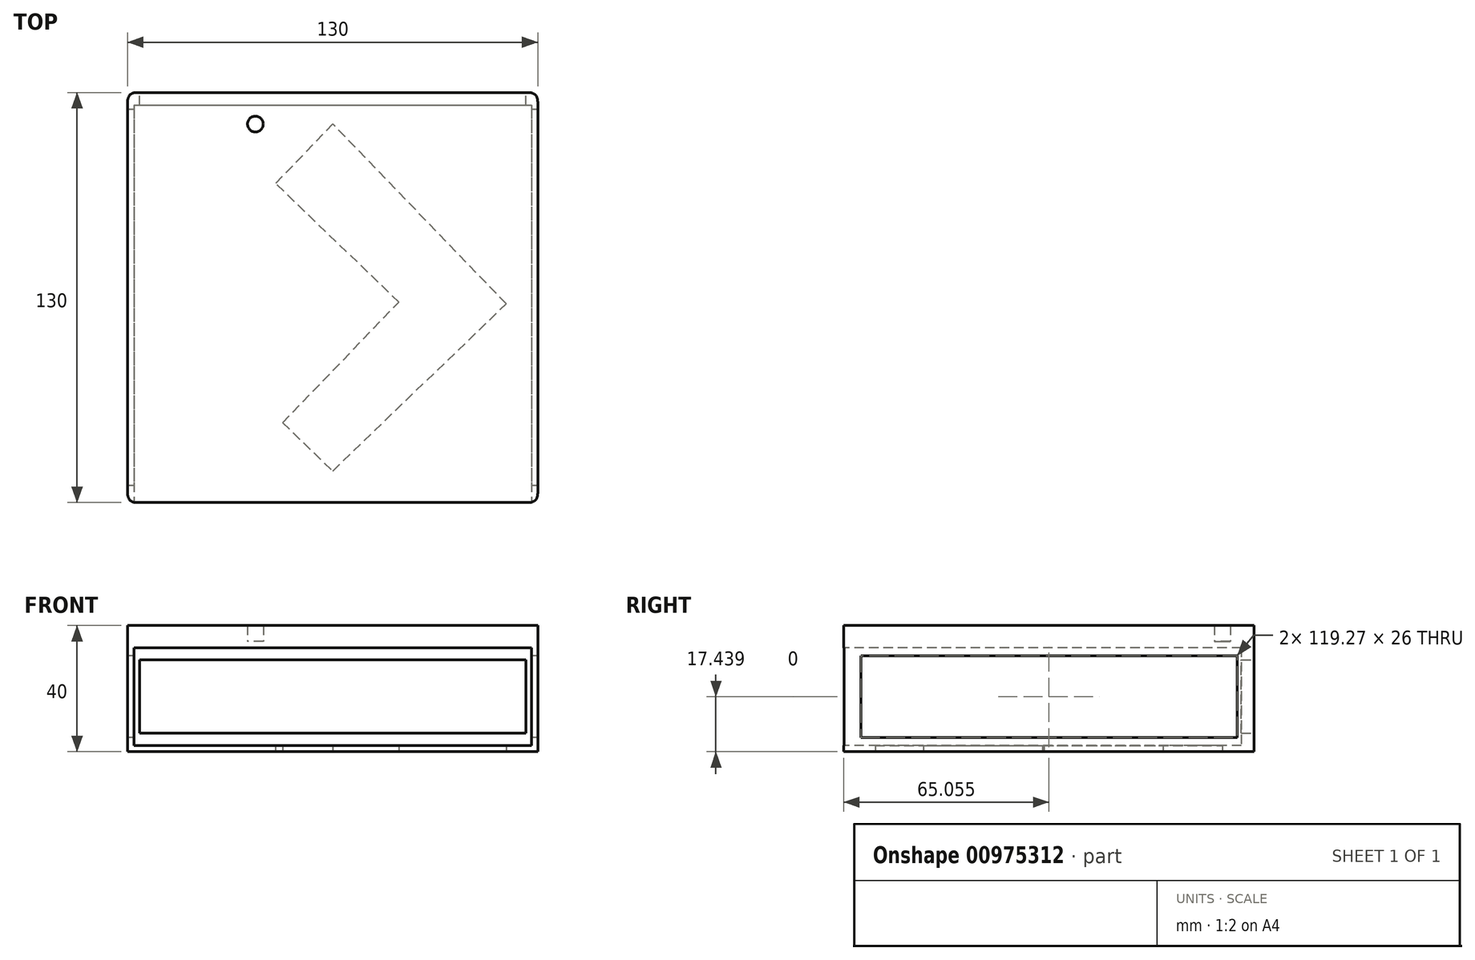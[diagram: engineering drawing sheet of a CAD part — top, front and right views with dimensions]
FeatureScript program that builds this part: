
annotation { "Feature Type Name" : "Feature", "Feature Type Description" : "" }
export const myFeature = defineFeature(function(context is Context, id is Id, definition is map)
    precondition{}
    {
        {
            var Q0;
            Q0=qCreatedBy(makeId("Top.planeOp"),FACE);
            var sketch = newSketch(context, id + "F0", { "sketchPlane" : qUnion([Q0])});
            skLineSegment(sketch, "E0.bottom", {"start": v(-63, 66.16) * mm, "end": v(67, 66.16) * mm});
            skLineSegment(sketch, "E0.top", {"start": v(-63, -63.84) * mm, "end": v(67, -63.84) * mm});
            skLineSegment(sketch, "E0.left", {"start": v(-63, 66.16) * mm, "end": v(-63, -63.84) * mm});
            skLineSegment(sketch, "E0.right", {"start": v(67, 66.16) * mm, "end": v(67, -63.84) * mm});
            skSolve(sketch);
        }
        {
            var Q0;
            Q0=makeQuery(id+"F0.imprint","IMPRINT",FACE,{"disambiguationData":[TD([[makeQuery(id+"F0.imprint","IMPRINT",EDGE,{"derivedFrom":sQuery(id+"F0.wireOp",EDGE,"E0.bottom")}),-1.0]])]});
            extrude(context, id + "F1", {"entities" : qUnion([Q0]), "endBound" : BoundingType.SYMMETRIC, "depth" : 35 * mm, "offsetDistance" : 25 * mm});
        }
        {
            var Q0;
            Q0=makeQuery(id+"F1.opExtrude","SWEPT_FACE",FACE,{"disambiguationData":[OSD([sQuery(id+"F0.wireOp",EDGE,"E0.top")])]});
            var sketch = newSketch(context, id + "F2", { "sketchPlane" : qUnion([Q0])});
            skLineSegment(sketch, "E1.bottom", {"start": v(-61, 15.5) * mm, "end": v(65, 15.5) * mm});
            skLineSegment(sketch, "E1.top", {"start": v(-61, -15.5) * mm, "end": v(65, -15.5) * mm});
            skLineSegment(sketch, "E1.left", {"start": v(-61, 15.5) * mm, "end": v(-61, -15.5) * mm});
            skLineSegment(sketch, "E1.right", {"start": v(65, 15.5) * mm, "end": v(65, -15.5) * mm});
            skSolve(sketch);
        }
        {
            var Q0;
            Q0=makeQuery(id+"F2.imprint","IMPRINT",FACE,{"disambiguationData":[TD([[makeQuery(id+"F2.imprint","IMPRINT",EDGE,{"derivedFrom":sQuery(id+"F2.wireOp",EDGE,"E1.bottom")}),-1.0]])]});
            extrude(context, id + "F3", {"entities" : qUnion([Q0]), "operationType" : NewBodyOperationType.REMOVE, "oppositeDirection" : true, "depth" : 126 * mm, "offsetDistance" : 25 * mm});
        }
        {
            var Q0;
            Q0=makeQuery(id+"F1.opExtrude","CAP_FACE",FACE,{"disambiguationData":[OSD([sQuery(id+"F0.wireOp",EDGE,"E0.bottom"),sQuery(id+"F0.wireOp",EDGE,"E0.top"),sQuery(id+"F0.wireOp",EDGE,"E0.left"),sQuery(id+"F0.wireOp",EDGE,"E0.right")])],"isStart":false});
            var sketch = newSketch(context, id + "F4", { "sketchPlane" : qUnion([Q0])});
            skCircle(sketch, "E2", {"center": v(-22.5, -53.84) * mm, "radius": 2.5 * mm});
            skLineSegment(sketch, "E3.bottom", {"start": v(-53, 56.16) * mm, "end": v(57, 56.16) * mm});
            skLineSegment(sketch, "E3.top", {"start": v(-53, -53.84) * mm, "end": v(57, -53.84) * mm});
            skLineSegment(sketch, "E3.left", {"start": v(-53, 56.16) * mm, "end": v(-53, -53.84) * mm});
            skLineSegment(sketch, "E3.right", {"start": v(57, 56.16) * mm, "end": v(57, -53.84) * mm});
            skLineSegment(sketch, "E4.bottom", {"start": v(-63, 66.16) * mm, "end": v(67, 66.16) * mm});
            skLineSegment(sketch, "E4.top", {"start": v(-63, -63.84) * mm, "end": v(67, -63.84) * mm});
            skLineSegment(sketch, "E4.left", {"start": v(-63, 66.16) * mm, "end": v(-63, -63.84) * mm});
            skLineSegment(sketch, "E4.right", {"start": v(67, 66.16) * mm, "end": v(67, -63.84) * mm});
            skCircle(sketch, "E5", {"center": v(-22.5, 56.16) * mm, "radius": 2.5 * mm});
            skCircle(sketch, "E6", {"center": v(22.5, 56.16) * mm, "radius": 2.5 * mm});
            skCircle(sketch, "E7", {"center": v(22.5, -53.84) * mm, "radius": 2.5 * mm});
            skCircle(sketch, "E8", {"center": v(57.01, -53.81) * mm, "radius": 2.5 * mm});
            skCircle(sketch, "E9", {"center": v(-53, 56.17) * mm, "radius": 2.5 * mm});
            skCircle(sketch, "E10", {"center": v(57, 56.17) * mm, "radius": 2.5 * mm});
            skCircle(sketch, "E11", {"center": v(-53, -53.84) * mm, "radius": 2.5 * mm});
            skSolve(sketch);
        }
        {
            var Q0;
            Q0=makeQuery(id+"F4.imprint","IMPRINT",FACE,{"disambiguationData":[TD([[makeQuery(id+"F4.imprint","IMPRINT",EDGE,{"derivedFrom":sQuery(id+"F4.wireOp",EDGE,"E2")}),1.0]])]});
            var Q1;
            {var subQ0=sQuery(id+"F4.wireOp",EDGE,"E5");var subQ1=sQuery(id+"F4.wireOp",EDGE,"E3.bottom");var subQ2=makeQuery(id+"F4.imprint","INTERSECT",VERTEX,{"disambiguationData":[OD(0.0)],"derivedFrom":[subQ1,subQ0]});Q1=makeQuery(id+"F4.imprint","IMPRINT",FACE,{"disambiguationData":[TD([[makeQuery(id+"F4.imprint","IMPRINT",EDGE,{"disambiguationData":[TD([[subQ2,-1.0]])],"derivedFrom":subQ1}),1.0]])]});}
            var Q2;
            {var subQ0=sQuery(id+"F4.wireOp",EDGE,"E5");var subQ1=sQuery(id+"F4.wireOp",EDGE,"E3.bottom");var subQ2=makeQuery(id+"F4.imprint","INTERSECT",VERTEX,{"disambiguationData":[OD(0.0)],"derivedFrom":[subQ1,subQ0]});Q2=makeQuery(id+"F4.imprint","IMPRINT",FACE,{"disambiguationData":[TD([[makeQuery(id+"F4.imprint","IMPRINT",EDGE,{"disambiguationData":[TD([[subQ2,-1.0]])],"derivedFrom":subQ1}),-1.0]])]});}
            var Q3;
            {var subQ0=sQuery(id+"F4.wireOp",EDGE,"E6");var subQ1=sQuery(id+"F4.wireOp",EDGE,"E3.bottom");var subQ2=makeQuery(id+"F4.imprint","INTERSECT",VERTEX,{"disambiguationData":[OD(0.0)],"derivedFrom":[subQ1,subQ0]});Q3=makeQuery(id+"F4.imprint","IMPRINT",FACE,{"disambiguationData":[TD([[makeQuery(id+"F4.imprint","IMPRINT",EDGE,{"disambiguationData":[TD([[subQ2,-1.0]])],"derivedFrom":subQ1}),1.0]])]});}
            var Q4;
            {var subQ0=sQuery(id+"F4.wireOp",EDGE,"E6");var subQ1=sQuery(id+"F4.wireOp",EDGE,"E3.bottom");var subQ2=makeQuery(id+"F4.imprint","INTERSECT",VERTEX,{"disambiguationData":[OD(0.0)],"derivedFrom":[subQ1,subQ0]});Q4=makeQuery(id+"F4.imprint","IMPRINT",FACE,{"disambiguationData":[TD([[makeQuery(id+"F4.imprint","IMPRINT",EDGE,{"disambiguationData":[TD([[subQ2,-1.0]])],"derivedFrom":subQ1}),-1.0]])]});}
            var Q5;
            {var subQ0=sQuery(id+"F4.wireOp",EDGE,"E7");var subQ1=sQuery(id+"F4.wireOp",EDGE,"E3.top");var subQ2=makeQuery(id+"F4.imprint","INTERSECT",VERTEX,{"disambiguationData":[OD(0.0)],"derivedFrom":[subQ1,subQ0]});Q5=makeQuery(id+"F4.imprint","IMPRINT",FACE,{"disambiguationData":[TD([[makeQuery(id+"F4.imprint","IMPRINT",EDGE,{"disambiguationData":[TD([[subQ2,-1.0]])],"derivedFrom":subQ1}),-1.0]])]});}
            var Q6;
            {var subQ0=sQuery(id+"F4.wireOp",EDGE,"E7");var subQ1=sQuery(id+"F4.wireOp",EDGE,"E3.top");var subQ2=makeQuery(id+"F4.imprint","INTERSECT",VERTEX,{"disambiguationData":[OD(0.0)],"derivedFrom":[subQ1,subQ0]});Q6=makeQuery(id+"F4.imprint","IMPRINT",FACE,{"disambiguationData":[TD([[makeQuery(id+"F4.imprint","IMPRINT",EDGE,{"disambiguationData":[TD([[subQ2,-1.0]])],"derivedFrom":subQ1}),1.0]])]});}
            var Q7;
            {var subQ0=sQuery(id+"F4.wireOp",EDGE,"E3.right");var subQ1=sQuery(id+"F4.wireOp",EDGE,"E3.bottom");var subQ2=makeQuery(id+"F4.imprint","INTERSECT",VERTEX,{"derivedFrom":[subQ1,subQ0]});Q7=makeQuery(id+"F4.imprint","IMPRINT",FACE,{"disambiguationData":[TD([[makeQuery(id+"F4.imprint","IMPRINT",EDGE,{"disambiguationData":[TD([[subQ2,1.0]])],"derivedFrom":subQ1}),-1.0]])]});}
            var Q8;
            {var subQ0=sQuery(id+"F4.wireOp",EDGE,"E3.right");var subQ1=sQuery(id+"F4.wireOp",EDGE,"E3.bottom");var subQ2=makeQuery(id+"F4.imprint","INTERSECT",VERTEX,{"derivedFrom":[subQ1,subQ0]});Q8=makeQuery(id+"F4.imprint","IMPRINT",FACE,{"disambiguationData":[TD([[makeQuery(id+"F4.imprint","IMPRINT",EDGE,{"disambiguationData":[TD([[subQ2,1.0]])],"derivedFrom":subQ1}),1.0]])]});}
            var Q9;
            {var subQ0=sQuery(id+"F4.wireOp",EDGE,"E3.right");var subQ1=sQuery(id+"F4.wireOp",EDGE,"E3.top");var subQ2=makeQuery(id+"F4.imprint","INTERSECT",VERTEX,{"derivedFrom":[subQ1,subQ0]});Q9=makeQuery(id+"F4.imprint","IMPRINT",FACE,{"disambiguationData":[TD([[makeQuery(id+"F4.imprint","IMPRINT",EDGE,{"disambiguationData":[TD([[subQ2,1.0]])],"derivedFrom":subQ1}),1.0]])]});}
            var Q10;
            {var subQ0=sQuery(id+"F4.wireOp",EDGE,"E3.right");var subQ1=sQuery(id+"F4.wireOp",EDGE,"E3.top");var subQ2=makeQuery(id+"F4.imprint","INTERSECT",VERTEX,{"derivedFrom":[subQ1,subQ0]});Q10=makeQuery(id+"F4.imprint","IMPRINT",FACE,{"disambiguationData":[TD([[makeQuery(id+"F4.imprint","IMPRINT",EDGE,{"disambiguationData":[TD([[subQ2,1.0]])],"derivedFrom":subQ1}),-1.0]])]});}
            var Q11;
            {var subQ0=sQuery(id+"F4.wireOp",EDGE,"E3.left");var subQ1=sQuery(id+"F4.wireOp",EDGE,"E3.top");var subQ2=makeQuery(id+"F4.imprint","INTERSECT",VERTEX,{"derivedFrom":[subQ1,subQ0]});Q11=makeQuery(id+"F4.imprint","IMPRINT",FACE,{"disambiguationData":[TD([[makeQuery(id+"F4.imprint","IMPRINT",EDGE,{"disambiguationData":[TD([[subQ2,-1.0]])],"derivedFrom":subQ1}),-1.0]])]});}
            var Q12;
            {var subQ0=sQuery(id+"F4.wireOp",EDGE,"E3.left");var subQ1=sQuery(id+"F4.wireOp",EDGE,"E3.top");var subQ2=makeQuery(id+"F4.imprint","INTERSECT",VERTEX,{"derivedFrom":[subQ1,subQ0]});Q12=makeQuery(id+"F4.imprint","IMPRINT",FACE,{"disambiguationData":[TD([[makeQuery(id+"F4.imprint","IMPRINT",EDGE,{"disambiguationData":[TD([[subQ2,-1.0]])],"derivedFrom":subQ1}),1.0]])]});}
            var Q13;
            {var subQ0=sQuery(id+"F4.wireOp",EDGE,"E3.left");var subQ1=sQuery(id+"F4.wireOp",EDGE,"E3.bottom");var subQ2=makeQuery(id+"F4.imprint","INTERSECT",VERTEX,{"derivedFrom":[subQ1,subQ0]});Q13=makeQuery(id+"F4.imprint","IMPRINT",FACE,{"disambiguationData":[TD([[makeQuery(id+"F4.imprint","IMPRINT",EDGE,{"disambiguationData":[TD([[subQ2,-1.0]])],"derivedFrom":subQ1}),-1.0]])]});}
            var Q14;
            {var subQ0=sQuery(id+"F4.wireOp",EDGE,"E3.left");var subQ1=sQuery(id+"F4.wireOp",EDGE,"E3.bottom");var subQ2=makeQuery(id+"F4.imprint","INTERSECT",VERTEX,{"derivedFrom":[subQ1,subQ0]});Q14=makeQuery(id+"F4.imprint","IMPRINT",FACE,{"disambiguationData":[TD([[makeQuery(id+"F4.imprint","IMPRINT",EDGE,{"disambiguationData":[TD([[subQ2,-1.0]])],"derivedFrom":subQ1}),1.0]])]});}
            extrude(context, id + "F5", {"entities" : qUnion([Q0, Q1, Q2, Q3, Q4, Q5, Q6, Q7, Q8, Q9, Q10, Q11, Q12, Q13, Q14]), "operationType" : NewBodyOperationType.ADD, "depth" : 5 * mm, "offsetDistance" : 25 * mm});
        }
        {
            var Q0;
            Q0=makeQuery(id+"F1.opExtrude","CAP_FACE",FACE,{"disambiguationData":[OSD([sQuery(id+"F0.wireOp",EDGE,"E0.bottom"),sQuery(id+"F0.wireOp",EDGE,"E0.top"),sQuery(id+"F0.wireOp",EDGE,"E0.left"),sQuery(id+"F0.wireOp",EDGE,"E0.right")])],"isStart":true});
            var sketch = newSketch(context, id + "F6", { "sketchPlane" : qUnion([Q0])});
            skLineSegment(sketch, "E12.bottom", {"start": v(-63, 63.84) * mm, "end": v(67, 63.84) * mm});
            skLineSegment(sketch, "E12.top", {"start": v(-63, -66.16) * mm, "end": v(67, -66.16) * mm});
            skLineSegment(sketch, "E12.left", {"start": v(-63, 63.84) * mm, "end": v(-63, -66.16) * mm});
            skLineSegment(sketch, "E12.right", {"start": v(67, 63.84) * mm, "end": v(67, -66.16) * mm});
            skLineSegment(sketch, "E13.bottom", {"start": v(-53, 53.84) * mm, "end": v(57, 53.84) * mm});
            skLineSegment(sketch, "E13.top", {"start": v(-53, -56.16) * mm, "end": v(57, -56.16) * mm});
            skLineSegment(sketch, "E13.left", {"start": v(-53, 53.84) * mm, "end": v(-53, -56.16) * mm});
            skLineSegment(sketch, "E13.right", {"start": v(57, 53.84) * mm, "end": v(57, -56.16) * mm});
            skLineSegment(sketch, "E14", {"start": v(-53, 0.84) * mm, "end": v(2, 53.84) * mm});
            skLineSegment(sketch, "E15", {"start": v(2, 53.84) * mm, "end": v(57, 0.84) * mm});
            skLineSegment(sketch, "E16", {"start": v(57, 0.84) * mm, "end": v(2.08, -56.16) * mm});
            skLineSegment(sketch, "E17", {"start": v(2.08, -56.16) * mm, "end": v(-53, 0.84) * mm});
            skLineSegment(sketch, "E18", {"start": v(-53, 0.84) * mm, "end": v(-35.06, 18.12) * mm});
            skLineSegment(sketch, "E19", {"start": v(-35.06, 18.12) * mm, "end": v(-18.4, 0.84) * mm});
            skLineSegment(sketch, "E20", {"start": v(-18.4, 0.84) * mm, "end": v(-36.32, -16.42) * mm});
            skLineSegment(sketch, "E21", {"start": v(-36.32, -16.42) * mm, "end": v(-53, 0.84) * mm});
            skLineSegment(sketch, "E22", {"start": v(-13.87, 38.54) * mm, "end": v(22.98, 0.3) * mm});
            skLineSegment(sketch, "E23", {"start": v(22.98, 0.3) * mm, "end": v(-16.1, -37.36) * mm});
            skSolve(sketch);
        }
        {
            var Q0;
            {var subQ3=sQuery(id+"F6.wireOp",EDGE,"E15");Q0=makeQuery(id+"F6.imprint","IMPRINT",FACE,{"disambiguationData":[TD([[makeQuery(id+"F6.imprint","IMPRINT",EDGE,{"derivedFrom":subQ3}),-1.0]])]});}
            var Q1;
            Q1=makeQuery(id+"F6.imprint","IMPRINT",FACE,{"disambiguationData":[TD([[makeQuery(id+"F6.imprint","IMPRINT",EDGE,{"derivedFrom":sQuery(id+"F6.wireOp",EDGE,"E18")}),-1.0]])]});
            var Q2;
            Q2=makeQuery(id+"F1.opExtrude","SWEPT_BODY",BODY,{"disambiguationData":[OSD([sQuery(id+"F0.wireOp",EDGE,"E0.bottom"),sQuery(id+"F0.wireOp",EDGE,"E0.top"),sQuery(id+"F0.wireOp",EDGE,"E0.left"),sQuery(id+"F0.wireOp",EDGE,"E0.right")])]});
            extrude(context, id + "F7", {"entities" : qUnion([Q0, Q1]), "operationType" : NewBodyOperationType.REMOVE, "oppositeDirection" : true, "depth" : 3 * mm, "endBoundEntityBody" : qUnion([Q2]), "offsetDistance" : 25 * mm});
        }
        {
            var Q0;
            Q0=makeQuery(id+"F1.opExtrude","SWEPT_FACE",FACE,{"disambiguationData":[OSD([sQuery(id+"F0.wireOp",EDGE,"E0.left")])]});
            var sketch = newSketch(context, id + "F8", { "sketchPlane" : qUnion([Q0])});
            skLineSegment(sketch, "E24.bottom", {"start": v(-60.85, 12.94) * mm, "end": v(58.42, 12.94) * mm});
            skLineSegment(sketch, "E24.top", {"start": v(-60.85, -13.06) * mm, "end": v(58.42, -13.06) * mm});
            skLineSegment(sketch, "E24.left", {"start": v(-60.85, 12.94) * mm, "end": v(-60.85, -13.06) * mm});
            skLineSegment(sketch, "E24.right", {"start": v(58.42, 12.94) * mm, "end": v(58.42, -13.06) * mm});
            skSolve(sketch);
        }
        {
            var Q0;
            Q0=makeQuery(id+"F1.opExtrude","SWEPT_FACE",FACE,{"disambiguationData":[OSD([sQuery(id+"F0.wireOp",EDGE,"E0.bottom")])]});
            var sketch = newSketch(context, id + "F9", { "sketchPlane" : qUnion([Q0])});
            skLineSegment(sketch, "E25.bottom", {"start": v(-63.2, 11.63) * mm, "end": v(59.19, 11.63) * mm});
            skLineSegment(sketch, "E25.top", {"start": v(-63.2, -11.63) * mm, "end": v(59.19, -11.63) * mm});
            skLineSegment(sketch, "E25.left", {"start": v(-63.2, 11.63) * mm, "end": v(-63.2, -11.63) * mm});
            skLineSegment(sketch, "E25.right", {"start": v(59.19, 11.63) * mm, "end": v(59.19, -11.63) * mm});
            skSolve(sketch);
        }
        {
            var Q0;
            Q0=makeQuery(id+"F9.imprint","IMPRINT",FACE,{"disambiguationData":[TD([[makeQuery(id+"F9.imprint","IMPRINT",EDGE,{"derivedFrom":sQuery(id+"F9.wireOp",EDGE,"E25.bottom")}),-1.0]])]});
            extrude(context, id + "F10", {"entities" : qUnion([Q0]), "operationType" : NewBodyOperationType.REMOVE, "oppositeDirection" : true, "depth" : 7 * mm, "offsetDistance" : 25 * mm});
        }
        {
            var Q0;
            Q0=makeQuery(id+"F8.imprint","IMPRINT",FACE,{"disambiguationData":[TD([[makeQuery(id+"F8.imprint","IMPRINT",EDGE,{"derivedFrom":sQuery(id+"F8.wireOp",EDGE,"E24.bottom")}),-1.0]])]});
            extrude(context, id + "F11", {"entities" : qUnion([Q0]), "operationType" : NewBodyOperationType.REMOVE, "oppositeDirection" : true, "depth" : 130 * mm, "offsetDistance" : 25 * mm});
        }
        {
            var Q0;
            Q0=makeQuery(id+"F1.opExtrude","SWEPT_EDGE",EDGE,{"disambiguationData":[OSD([sQuery(id+"F0.wireOp",EDGE,"E0.bottom"),sQuery(id+"F0.wireOp",EDGE,"E0.left")])]});
            var Q1;
            Q1=makeQuery(id+"F1.opExtrude","SWEPT_EDGE",EDGE,{"disambiguationData":[OSD([sQuery(id+"F0.wireOp",EDGE,"E0.top"),sQuery(id+"F0.wireOp",EDGE,"E0.left")])]});
            var Q2;
            Q2=makeQuery(id+"F1.opExtrude","SWEPT_EDGE",EDGE,{"disambiguationData":[OSD([sQuery(id+"F0.wireOp",EDGE,"E0.bottom"),sQuery(id+"F0.wireOp",EDGE,"E0.right")])]});
            var Q3;
            Q3=makeQuery(id+"F1.opExtrude","SWEPT_EDGE",EDGE,{"disambiguationData":[OSD([sQuery(id+"F0.wireOp",EDGE,"E0.top"),sQuery(id+"F0.wireOp",EDGE,"E0.right")])]});
            fillet(context, id + "F12", {"entities" : qUnion([Q0, Q1, Q2, Q3]), "radius" : 3 * mm, "tangentPropagation" : true, "rho" : 0.5, "crossSection" : FilletCrossSection.CONIC, "allowEdgeOverflow" : false});
        }
    });
